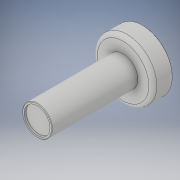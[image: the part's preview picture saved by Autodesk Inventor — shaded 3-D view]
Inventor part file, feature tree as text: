
AUTODESK INVENTOR PART (.ipt)
format: ipt  version: 2019 (Build 230136000, 136)  size: 131,584 bytes
history: native  units: mm
features: extrude x3, sketch x3, chamfer x2, fillet x1
ambient origin geometry x8: Origin, YZ Plane, XZ Plane, XY Plane, X Axis, Y Axis, Z Axis, Center Point
bodies: Solid1 (feature_tree)
feature tree (9):
  extrude  "Extrusion1"  Depth=10.0mm TaperAngle=0.0deg
  extrude  "Extrusion2"  Depth=43.2mm TaperAngle=0.0deg
  extrude  "Extrusion3"  Depth=1.0mm TaperAngle=0.0deg
  fillet  "Fillet1"  Radius=2.0mm
  chamfer  "Chamfer1"  Distance=2.0mm Angle=45.0deg
  chamfer  "Chamfer2"  Distance=2.0mm Angle=45.0deg
  sketch  "Sketch1"  dims[d0=30.0mm d1=10.0mm d2=0.0mm]
  sketch  "Sketch2"  dims[d3=15.0mm d4=43.2mm d5=0.0mm]
  sketch  "Sketch3"  dims[d6=1.0mm d7=1.0mm d8=0.0mm d9=2.0mm d10=0.25mm d11=2.0mm d12=45.0deg d13=0.25mm d14=2.0mm d15=45.0deg]
